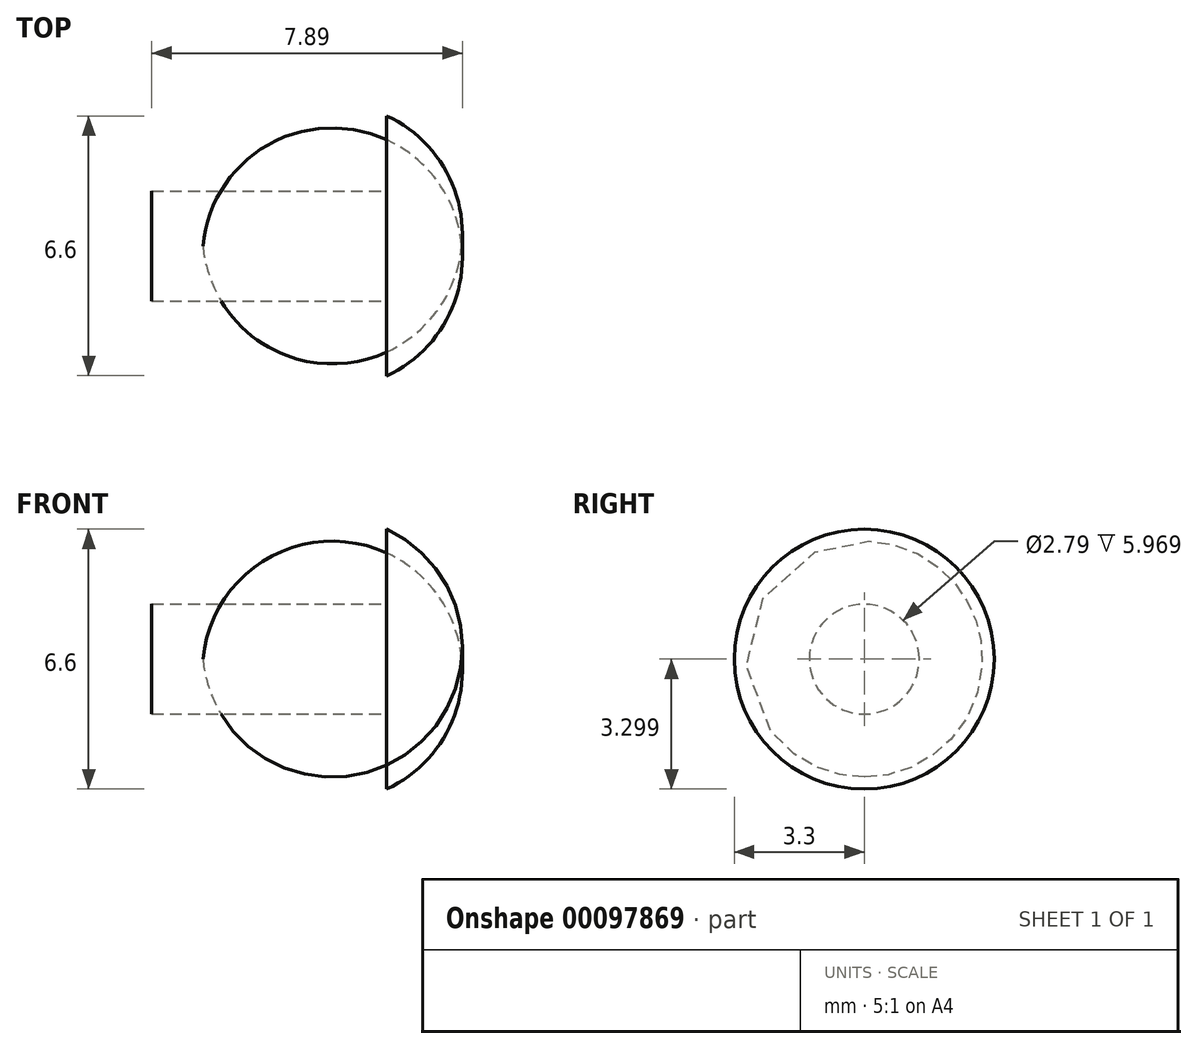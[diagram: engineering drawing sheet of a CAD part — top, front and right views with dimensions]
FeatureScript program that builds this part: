
annotation { "Feature Type Name" : "Feature", "Feature Type Description" : "" }
export const myFeature = defineFeature(function(context is Context, id is Id, definition is map)
    precondition{}
    {
        {
            var Q0;
            Q0=qCreatedBy(makeId("Front.planeOp"),FACE);
            var sketch = newSketch(context, id + "F0", { "sketchPlane" : qUnion([Q0])});
            skLineSegment(sketch, "E0", {"start": v(-53.43, 12.76) * mm, "end": v(-53.43, 9.46) * mm});
            skLineSegment(sketch, "E1", {"start": v(-53.43, 12.76) * mm, "end": v(-51.52, 12.76) * mm});
            skArc(sketch, "E2", {"start": v(-53.43, 9.46) * mm, "mid": v(-51.95, 10.8) * mm, "end": v(-51.52, 12.76) * mm});
            skSolve(sketch);
        }
        {
            var Q0;
            Q0=qSketchRegion(id+"F0",true);
            var Q1;
            Q1=sQuery(id+"F0.wireOp",EDGE,"E1");
            revolve(context, id + "F1", {"entities" : qUnion([Q0]), "axis" : qUnion([Q1]), "revolveType" : RevolveType.FULL});
        }
        {
            var Q0;
            Q0=makeQuery(id+"F1.opRevolve","SWEPT_FACE",FACE,{"disambiguationData":[OSD([sQuery(id+"F0.wireOp",EDGE,"E0")])]});
            var sketch = newSketch(context, id + "F2", { "sketchPlane" : qUnion([Q0])});
            skCircle(sketch, "E3", {"center": v(0, 12.76) * mm, "radius": 1.4 * mm});
            skSolve(sketch);
        }
        {
            var Q0;
            Q0=qSketchRegion(id+"F2",true);
            extrude(context, id + "F3", {"entities" : qUnion([Q0]), "operationType" : NewBodyOperationType.ADD, "depth" : 5.97 * mm});
        }
    });
